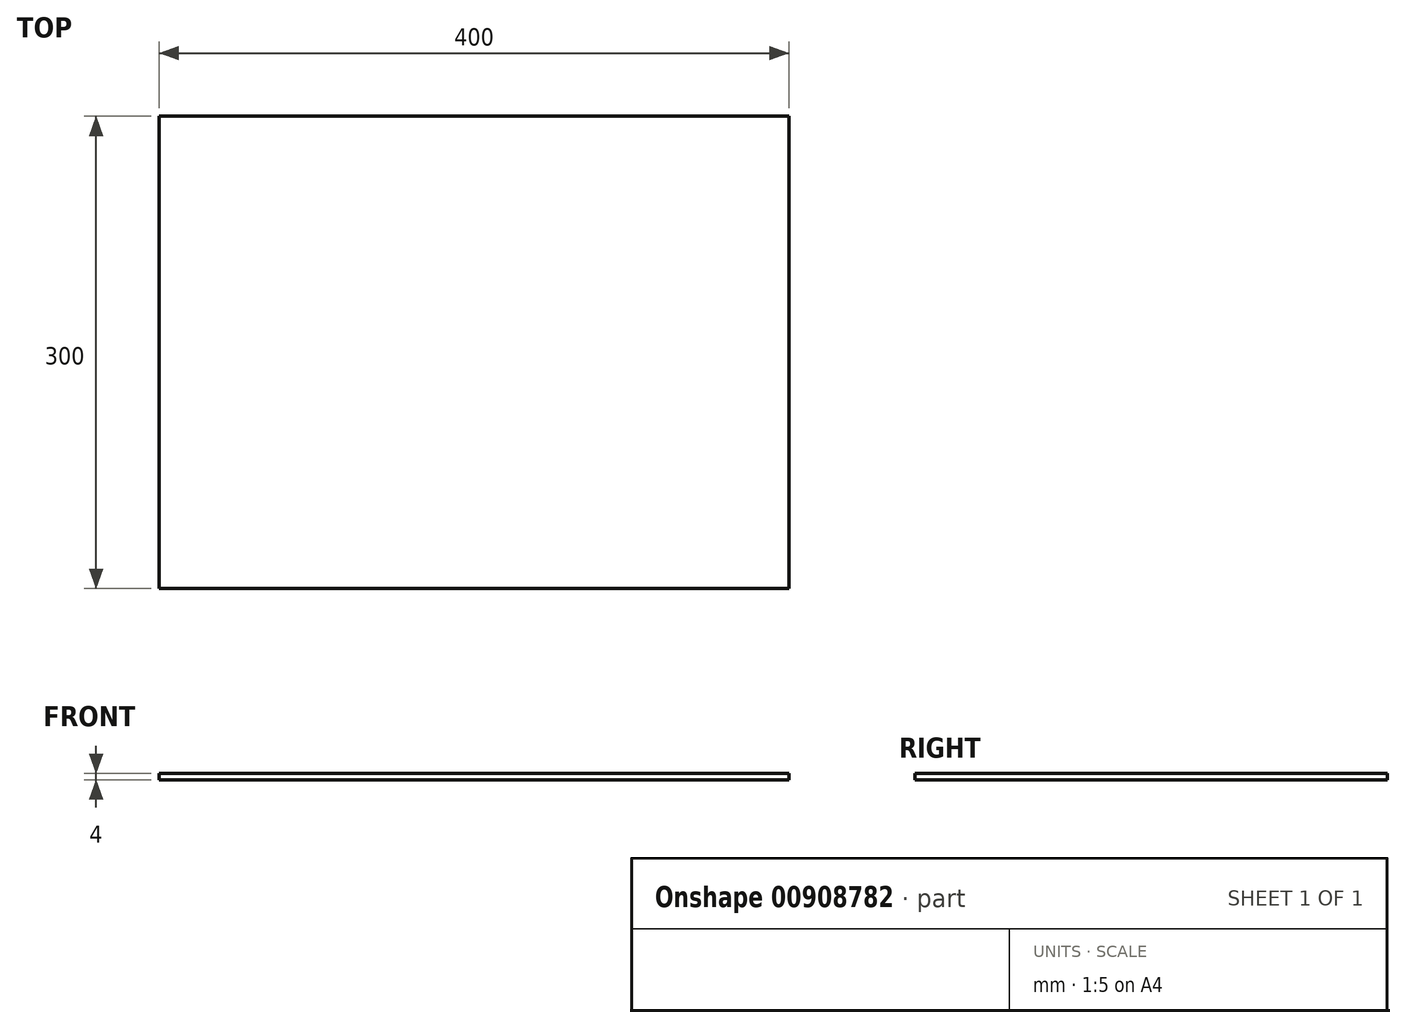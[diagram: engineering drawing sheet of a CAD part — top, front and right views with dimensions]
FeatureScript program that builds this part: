
annotation { "Feature Type Name" : "Feature", "Feature Type Description" : "" }
export const myFeature = defineFeature(function(context is Context, id is Id, definition is map)
    precondition{}
    {
        {
            var Q0;
            Q0=qCreatedBy(makeId("Top.planeOp"),FACE);
            var sketch = newSketch(context, id + "F0", { "sketchPlane" : qUnion([Q0])});
            skLineSegment(sketch, "E0.bottom", {"start": v(-200, 150) * mm, "end": v(200, 150) * mm});
            skLineSegment(sketch, "E0.top", {"start": v(-200, -150) * mm, "end": v(200, -150) * mm});
            skLineSegment(sketch, "E0.left", {"start": v(-200, 150) * mm, "end": v(-200, -150) * mm});
            skLineSegment(sketch, "E0.right", {"start": v(200, 150) * mm, "end": v(200, -150) * mm});
            skSolve(sketch);
        }
        {
            var Q0;
            Q0 = qSketchRegion(id + "F0", true);
            extrude(context, id + "F1", {"entities" : qUnion([Q0]), "oppositeDirection" : true, "depth" : 4 * mm, "offsetDistance" : 25 * mm});
        }
    });
